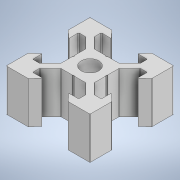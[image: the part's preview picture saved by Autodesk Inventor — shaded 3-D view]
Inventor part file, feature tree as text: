
AUTODESK INVENTOR PART (.ipt)
format: ipt  version: 2021 (Build 250183000, 183)  size: 234,496 bytes
history: native  units: mm
features: sketch x3, extrude x2, fillet x2, other x1, pattern_circular x1, hole x1, projected_geometry x1
ambient origin geometry x8: Origin, YZ Plane, XZ Plane, XY Plane, X Axis, Y Axis, Z Axis, Center Point
bodies: Body1 (feature_tree)
feature tree (11):
  other  "實體1"
  extrude  "擠出1"  Depth=20.0mm
  extrude  "擠出2"  Depth=20.0mm
  fillet  "圓角1"  Radius=10.0mm
  pattern_circular  "環形陣列1"  [2 undecoded]
  hole  "孔1"  [1 undecoded]
  fillet  "圓角2"  Radius=6.2mm
  sketch  "草圖1"
  sketch  "草圖2"
  projected_geometry  "投影迴路1"
  sketch  "草圖3"
note: 3 required parameter values undecoded (feature->parameter linkage not recoverable at this tier; creation-order binding heuristic only, values carry confidence <= 0.55)
